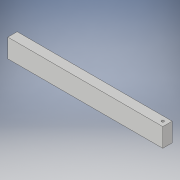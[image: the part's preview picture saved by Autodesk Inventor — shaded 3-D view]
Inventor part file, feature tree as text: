
AUTODESK INVENTOR PART (.ipt)
format: ipt  version: 2017 (Build 210142000, 142)  size: 95,232 bytes
history: native  units: in
note: dims shown in document units (in); Inventor stores cm internally (conversion verified against a paired STEP export)
features: extrude x1, hole x1, sketch x1
ambient origin geometry x8: Origin, YZ Plane, XZ Plane, XY Plane, X Axis, Y Axis, Z Axis, Center Point
bodies: Solid1 (feature_tree)
feature tree (3):
  extrude  "Extrusion1"  Depth=2.0in
  hole  "Hole1"  [1 undecoded]
  sketch  "Sketch1"  dims[d0=16.5in d1=2.0in d2=1.0in d3=0.0in d4=0.5in d5=0.5in d6=0.25in d7=0.75in d8=0.375in d9=0.25in d10=0.5635in d11=1.0in d12=0.8108in]
note: 1 required parameter value undecoded (feature->parameter linkage not recoverable at this tier; creation-order binding heuristic only, values carry confidence <= 0.55)
